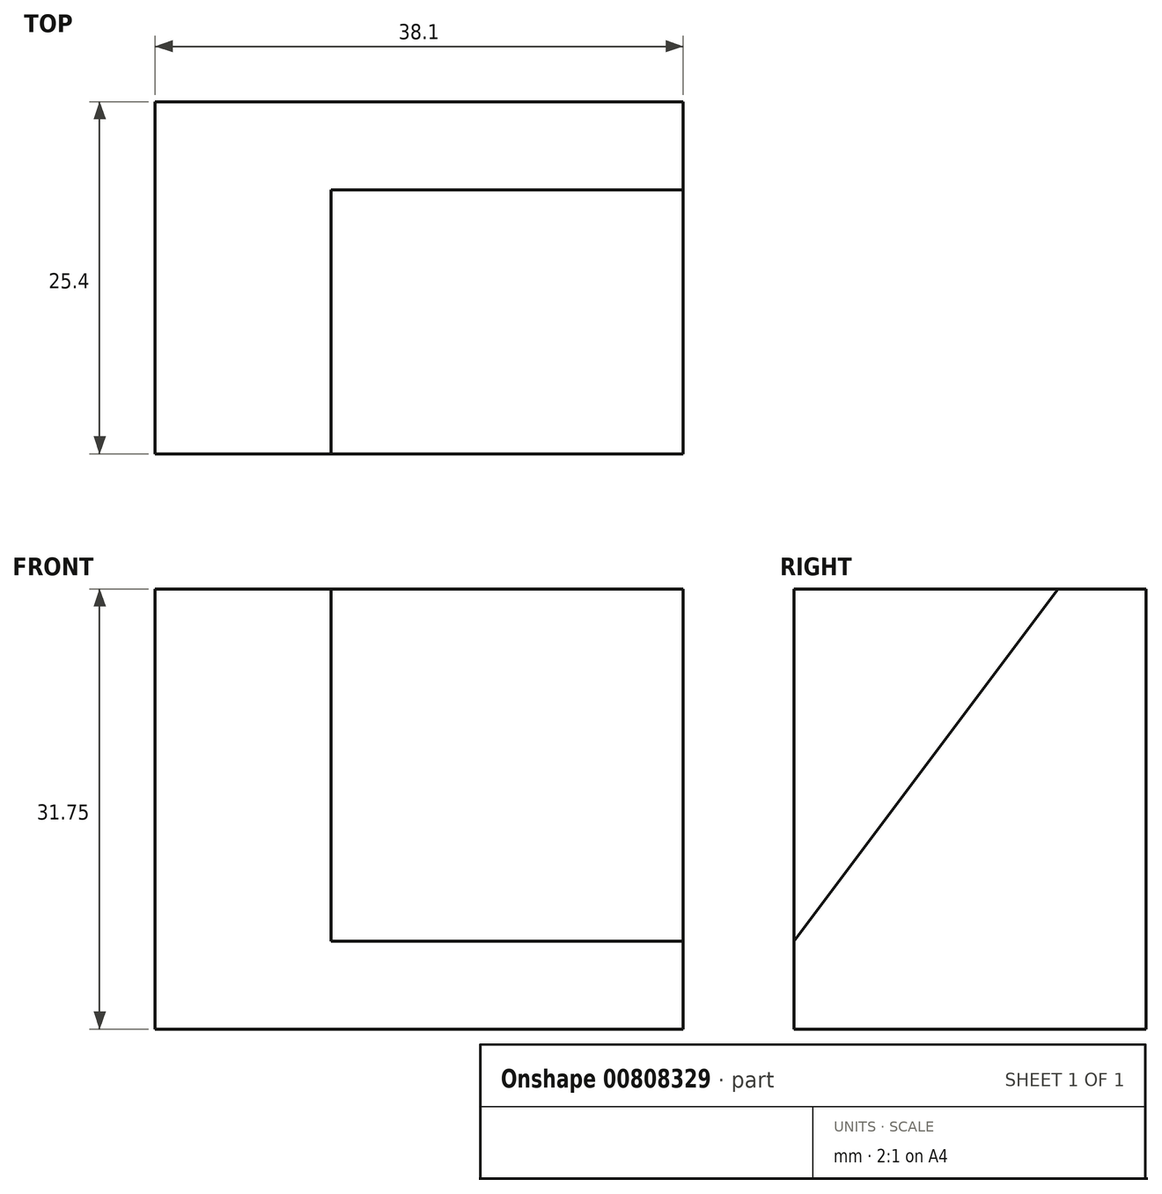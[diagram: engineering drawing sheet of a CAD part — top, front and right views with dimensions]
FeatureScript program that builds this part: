
annotation { "Feature Type Name" : "Feature", "Feature Type Description" : "" }
export const myFeature = defineFeature(function(context is Context, id is Id, definition is map)
    precondition{}
    {
        {
            var Q0;
            Q0=qCreatedBy(makeId("Top.planeOp"),FACE);
            var sketch = newSketch(context, id + "F0", { "sketchPlane" : qUnion([Q0])});
            skLineSegment(sketch, "E0.bottom", {"start": v(0, 0) * mm, "end": v(38.1, 0) * mm});
            skLineSegment(sketch, "E0.top", {"start": v(0, 25.4) * mm, "end": v(38.1, 25.4) * mm});
            skLineSegment(sketch, "E0.left", {"start": v(0, 0) * mm, "end": v(0, 25.4) * mm});
            skLineSegment(sketch, "E0.right", {"start": v(38.1, 0) * mm, "end": v(38.1, 25.4) * mm});
            skSolve(sketch);
        }
        {
            var Q0;
            Q0 = qSketchRegion(id + "F0", true);
            extrude(context, id + "F1", {"entities" : qUnion([Q0]), "depth" : 31.75 * mm, "offsetDistance" : 25.4 * mm});
        }
        {
            var Q0;
            Q0=makeQuery(id+"F1.opExtrude","SWEPT_FACE",FACE,{"disambiguationData":[OSD([sQuery(id+"F0.wireOp",EDGE,"E0.right")])]});
            var sketch = newSketch(context, id + "F2", { "sketchPlane" : qUnion([Q0])});
            skLineSegment(sketch, "E1", {"start": v(25.4, 31.75) * mm, "end": v(19.05, 31.75) * mm});
            skLineSegment(sketch, "E2", {"start": v(0, 0) * mm, "end": v(0, 6.35) * mm});
            skLineSegment(sketch, "E3", {"start": v(0, 6.35) * mm, "end": v(19.05, 31.75) * mm});
            skSolve(sketch);
        }
        {
            var Q0;
            Q0 = qSketchRegion(id + "F2", true);
            var Q1;
            {var subQ0=sQuery(id+"F2.wireOp",EDGE,"E3");Q1=makeQuery(id+"F2.imprint","IMPRINT",FACE,{"disambiguationData":[TD([[makeQuery(id+"F2.imprint","IMPRINT",EDGE,{"derivedFrom":subQ0}),1.0]])]});}
            extrude(context, id + "F3", {"entities" : qUnion([Q0, Q1]), "operationType" : NewBodyOperationType.REMOVE, "oppositeDirection" : true, "depth" : 25.4 * mm, "offsetDistance" : 25.4 * mm});
        }
    });
